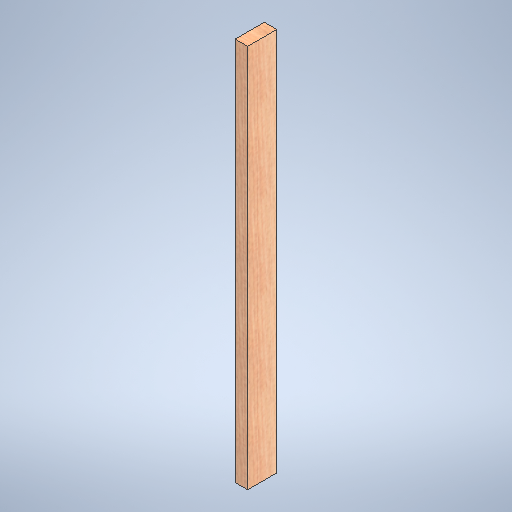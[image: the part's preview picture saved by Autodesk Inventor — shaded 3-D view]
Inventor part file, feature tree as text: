
AUTODESK INVENTOR PART (.ipt)
format: ipt  version: 2025.1 (Build 291241020, 241B)  size: 305,152 bytes
history: native  units: in
note: dims shown in document units (in); Inventor stores cm internally (conversion verified against a paired STEP export)
features: extrude x1, sketch x1
ambient origin geometry x8: Origin, YZ Plane, XZ Plane, XY Plane, X Axis, Y Axis, Z Axis, Center Point
bodies: Solid1 (feature_tree)
feature tree (2):
  extrude  "Extrusion1"  Depth=1.5in
  sketch  "Sketch1"  dims[d0=3.5in d1=1.5in d2=46.0in d3=0.0in]
